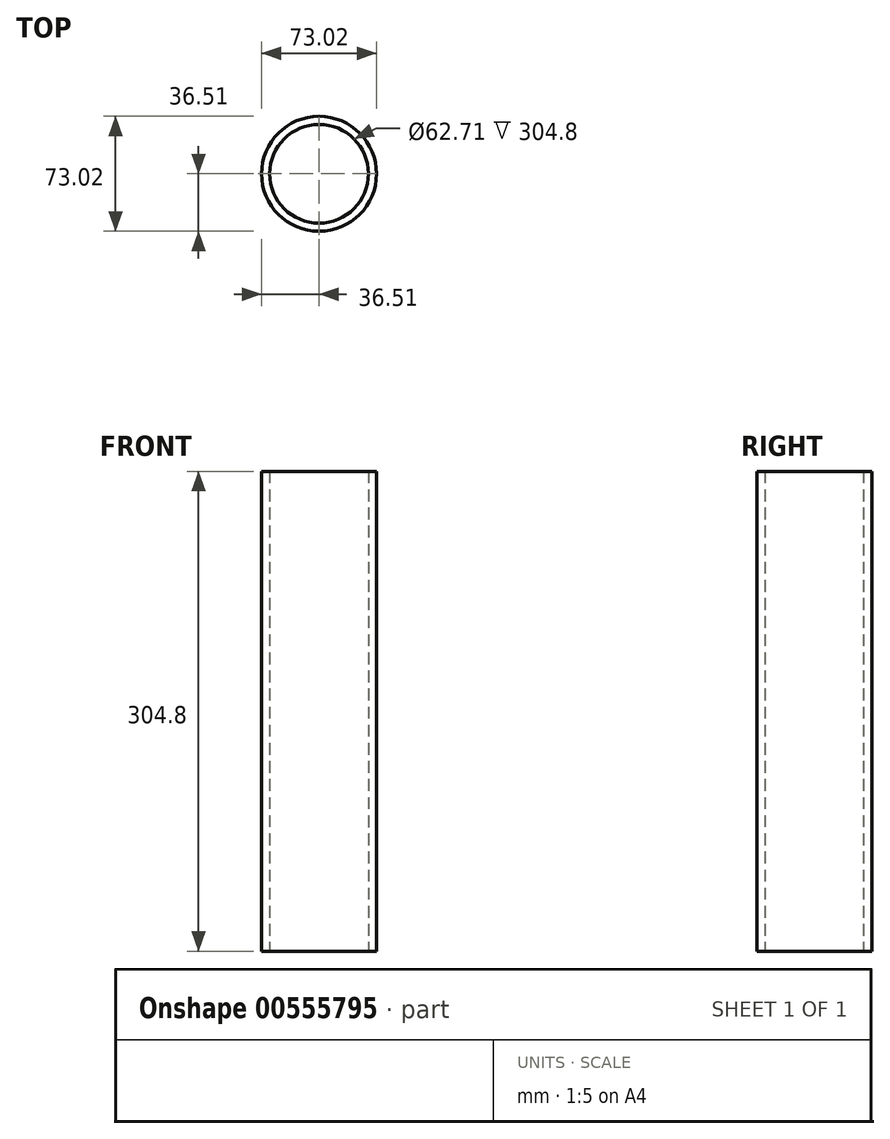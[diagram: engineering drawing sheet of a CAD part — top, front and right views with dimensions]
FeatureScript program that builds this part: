
annotation { "Feature Type Name" : "Feature", "Feature Type Description" : "" }
export const myFeature = defineFeature(function(context is Context, id is Id, definition is map)
    precondition{}
    {
        {
            var Q0;
            Q0=qCreatedBy(makeId("Top.planeOp"),FACE);
            var sketch = newSketch(context, id + "F0", { "sketchPlane" : qUnion([Q0])});
            skCircle(sketch, "E0", {"center": v(0, 0) * mm, "radius": 36.51 * mm});
            skCircle(sketch, "E1", {"center": v(0, 0) * mm, "radius": 31.36 * mm});
            skSolve(sketch);
        }
        {
            var Q0;
            Q0 = qSketchRegion(id + "F0", true);
            extrude(context, id + "F1", {"entities" : qUnion([Q0]), "depth" : 304.8 * mm, "offsetDistance" : 25.4 * mm});
        }
    });
